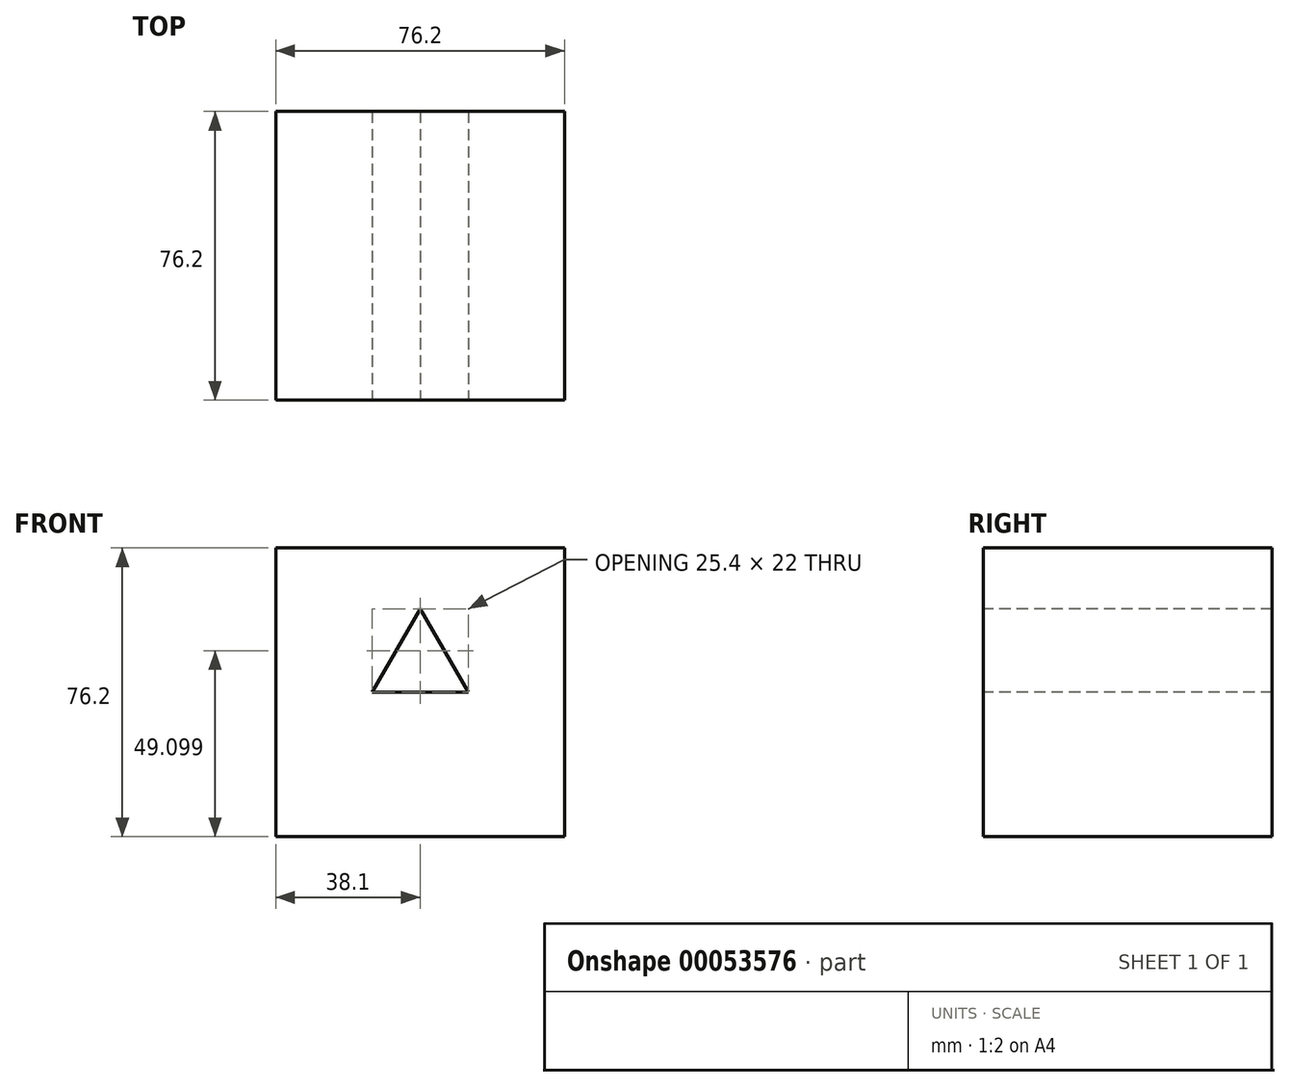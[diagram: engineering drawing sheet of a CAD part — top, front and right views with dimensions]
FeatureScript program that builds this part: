
annotation { "Feature Type Name" : "Feature", "Feature Type Description" : "" }
export const myFeature = defineFeature(function(context is Context, id is Id, definition is map)
    precondition{}
    {
        {
            var Q0;
            Q0=qCreatedBy(makeId("Front.planeOp"),FACE);
            var sketch = newSketch(context, id + "F0", { "sketchPlane" : qUnion([Q0])});
            skLineSegment(sketch, "E0.rect.bottom", {"start": v(38.1, -38.1) * mm, "end": v(-38.1, -38.1) * mm});
            skLineSegment(sketch, "E0.rect.top", {"start": v(38.1, 38.1) * mm, "end": v(-38.1, 38.1) * mm});
            skLineSegment(sketch, "E0.rect.left", {"start": v(38.1, -38.1) * mm, "end": v(38.1, 38.1) * mm});
            skLineSegment(sketch, "E0.rect.right", {"start": v(-38.1, -38.1) * mm, "end": v(-38.1, 38.1) * mm});
            skPoint(sketch, "E0.rect.middle", {"position": v(0, 0) * mm});
            skSolve(sketch);
        }
        {
            var Q0;
            Q0 = qSketchRegion(id + "F0", true);
            extrude(context, id + "F1", {"entities" : qUnion([Q0]), "endBound" : BoundingType.SYMMETRIC, "depth" : 76.2 * mm});
        }
        {
            var Q0;
            Q0=makeQuery(id+"F1.opExtrude","CAP_FACE",FACE,{"disambiguationData":[OSD([sQuery(id+"F0.wireOp",EDGE,"E0.rect.bottom"),sQuery(id+"F0.wireOp",EDGE,"E0.rect.top"),sQuery(id+"F0.wireOp",EDGE,"E0.rect.left"),sQuery(id+"F0.wireOp",EDGE,"E0.rect.right")])],"isStart":false});
            var sketch = newSketch(context, id + "F2", { "sketchPlane" : qUnion([Q0])});
            skLineSegment(sketch, "E1", {"start": v(-12.7, 0) * mm, "end": v(12.7, 0) * mm});
            skLineSegment(sketch, "E2", {"start": v(-12.7, 0) * mm, "end": v(0, 22) * mm});
            skLineSegment(sketch, "E3", {"start": v(0, 22) * mm, "end": v(12.7, 0) * mm});
            skSolve(sketch);
        }
        {
            var Q0;
            Q0 = qSketchRegion(id + "F2", true);
            extrude(context, id + "F3", {"entities" : qUnion([Q0]), "operationType" : NewBodyOperationType.REMOVE, "endBound" : BoundingType.THROUGH_ALL, "oppositeDirection" : true, "depth" : 76.2 * mm});
        }
    });
